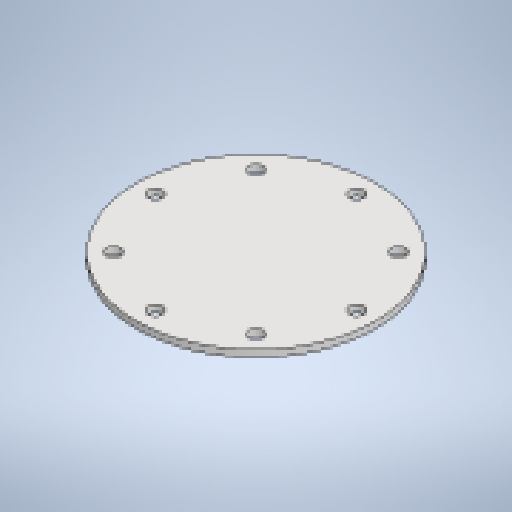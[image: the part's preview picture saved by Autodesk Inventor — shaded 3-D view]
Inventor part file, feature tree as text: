
AUTODESK INVENTOR PART (.ipt)
format: ipt  version: 2025.1 (Build 291241020, 241B)  size: 195,072 bytes
history: native  units: mm
features: other x3, sketch x2, sheet_metal_op x1, pattern_circular x1
ambient origin geometry x8: Origin, YZ Plane, XZ Plane, XY Plane, X Axis, Y Axis, Z Axis, Center Point
bodies: Body1 (feature_tree)
feature tree (7):
  sheet_metal_op  "Face2"
  pattern_circular  "Circular Pattern1"  [2 undecoded]
  sketch  "Sketch2"  dims[d14=8.0mm]
  other  "Plate2"
  sketch  "Sketch3"  dims[d15=17.0mm d17=8.0mm d18=0.0mm d19=80.0mm d20=360.0deg d25=161.0mm d27=285.0mm d28=240.0mm]
  other  "Cut1"
  other  "Definition1"
note: 2 required parameter values undecoded (feature->parameter linkage not recoverable at this tier; creation-order binding heuristic only, values carry confidence <= 0.55)
